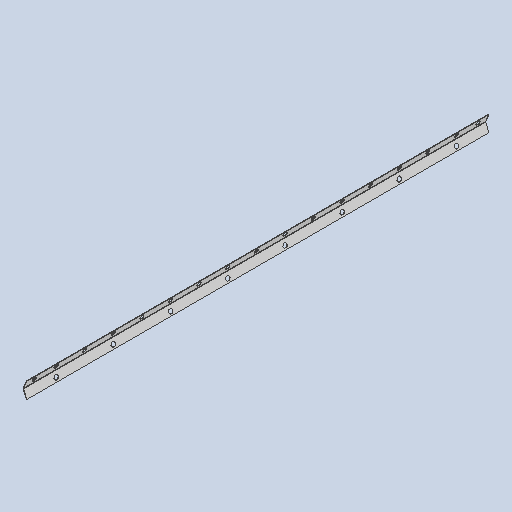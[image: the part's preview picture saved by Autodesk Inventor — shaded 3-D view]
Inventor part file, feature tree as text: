
AUTODESK INVENTOR PART (.ipt)
format: ipt  version: 2025 (Build 290162010, 162A)  size: 397,824 bytes
history: native  units: mm
features: sketch x4, sheet_metal_op x3, extrude x3, pattern_linear x2, other x2, mirror x1
ambient origin geometry x8: Origin, YZ Plane, XZ Plane, XY Plane, X Axis, Y Axis, Z Axis, Center Point
bodies: Body1 (feature_tree)
feature tree (15):
  sheet_metal_op  "Contour Flange1"
  extrude  "Extrusion1"  Depth=36.26mm
  extrude  "Extrusion6"  Depth=2.0mm
  mirror  "Mirror1"
  pattern_linear  "Rectangular Pattern4"  Spacing1=4.0mm  [1 undecoded]
  extrude  "Extrusion7"  Depth=2.0mm
  pattern_linear  "Rectangular Pattern5"  Count1=202  [1 undecoded]
  sketch  "Sketch4"  dims[d16=511.0mm d23=36.26mm]
  other  "Plate3"
  sheet_metal_op  "Bend2"
  sheet_metal_op  "Corner2"
  sketch  "Sketch6"  dims[d24=4.0mm d25=2.0mm]
  sketch  "Sketch12"  dims[d26=2.0mm]
  sketch  "Sketch13"  dims[d27=1.0mm d28=4.0mm d29=2.0mm d30=2020.0mm d31=2.0mm d32=3.0mm d33=8.0mm d34=2.0mm d35=2.0mm d36=11.0mm d41=11.0mm d42=10.0mm d43=0.0mm d75=50.0mm d76=25.0mm d77=125.0mm d78=0.0mm d79=0.0mm d80=80.0mm d82=250.0mm d83=11.0mm d84=0.0mm d85=0.0mm d86=70.0mm d88=250.0mm d93=19.22mm d94=40.75mm d95=19.22mm d96=40.75mm d97=16.8mm d98=16.8mm d99=16.8mm]
  other  "Definition1"
note: 2 required parameter values undecoded (feature->parameter linkage not recoverable at this tier; creation-order binding heuristic only, values carry confidence <= 0.55)
